# Revit family: IS_Tonicll_R4337_BIM_FR
name_source: partatom
category: Plumbing Fixtures
revit_build: Autodesk Revit 2017 (Build: 20160225_1515(x64)
units: mm (PartAtom-declared; Revit-internal decimal feet)

## family parameters
Always vertical = No
Cut with Voids When Loaded = No
OmniClass Number = 23.40.20.00
OmniClass Title = General Furniture and Specialties
Part Type = Normal
Room Calculation Point = No
Round Connector Dimension = Use Diameter
Shared = No
Work Plane-Based = No

## types (1)
- R4337WG - TONIC II SEPARATEUR
    Accessoires = www.idealspec.fr
    Auteur = Ideal Standard
    BIMobject category = Storage
    BIMobject category code = sanitary-storage
    BIMobject main category = Sanitary
    BIMobject main category code = sanitary
    BOSUseNativeGeometries = 1
    Bim-NomDuProjet = ISI_IdealStandard_VanityUnits_TONIC_R4337WG
    Brand url = www.idealspec.fr
    Caractéristiques = TONIC II DIVIDER GLS WHT
    CodeBarre = 3391500573130
    Conformité = NF
    ConseilsDInstallation = 0
    Cost = 0 $
    Couleur = Blanc
    CoûtDeRemplacement = 0
    Date of publishing = 2018_07_24
    DateDeCréation = 2018_07_24
    Description = TONIC II Séparateur
    Dimensions = 271 x 220 x 40 mm
    EAN code = https://3391500573130
    Edition number = 1
    Espace = Interne
    Finition = Blanc
    Forme = Complexe
    Hauteur = 271 mm  [stored 0.889108 ft]
    IfcExportAs = FURNITURE
    IfcExportType = IfcSanitaryTerminalType
    InformationsProduit = www.idealspec.fr
    Installation instructions = http://www.idealspec.fr
    Largeur = 220 mm  [stored 0.721785 ft]
    Longueur = 40 mm  [stored 0.131234 ft]
    Manufacturer name = Ideal Standard
    Marque = Ideal Standard
    Model = R4337WG
    NBS Reference Code = 35-75-94
    NBS Reference Description = Vanity Units
    Nominal height = 40
    Nominal width = 220
    Product Guid = 1c0d2299-1f30-4dd3-9dda-262a88a59fc7
    Product SKU = R4337
    Product certification = http://www.idealspec.fr
    Product data url = https://bimobject.com
    Product family = TONIC II
    Product group = Furniture
    Product name = TONIC II DIVIDER GLS WHT
    Product url = http://www.idealspec.fr
    Profondeur = 0 mm  [stored 0 ft]
    QR code = http://bimobject.com
    Raccordement = Plomberie
    Révision = 1
    Technical description = http://www.idealspec.fr
    URL = www.idealspec.fr
    Uniclass 1.4 Code = L72121
    Uniclass 1.4 Description = Vanity units
    Uniclass 2.0 Code = PR-35-75-94
    Uniclass 2.0 Description = Vanity Units
    Uniclass 2015 Code = Pr_40_20_76_94
    Uniclass 2015 Name = Vanity units
    Uniclass2015Code = Pr_40_20_76_94
    Uniclass2015Title = Vanity units
    Uniclass2015Version = Products v1.1
    UnitéDeMesure = Millimètres
    UnitéDeTemps = An
    UnitéMonétaire = €
    UrlDuFabricant = www.idealspec.fr
    Version = 1
    Weight Net (Kg) = 1
    Youtube clip = http://www.idealspec.fr

note: [stored X ft] marks values corroborated as IEEE doubles in the binary element streams (Revit-internal decimal feet)

## geometry (parser evidence)
native form markers: Sweep x2
no freeform markers — native parametric forms only
